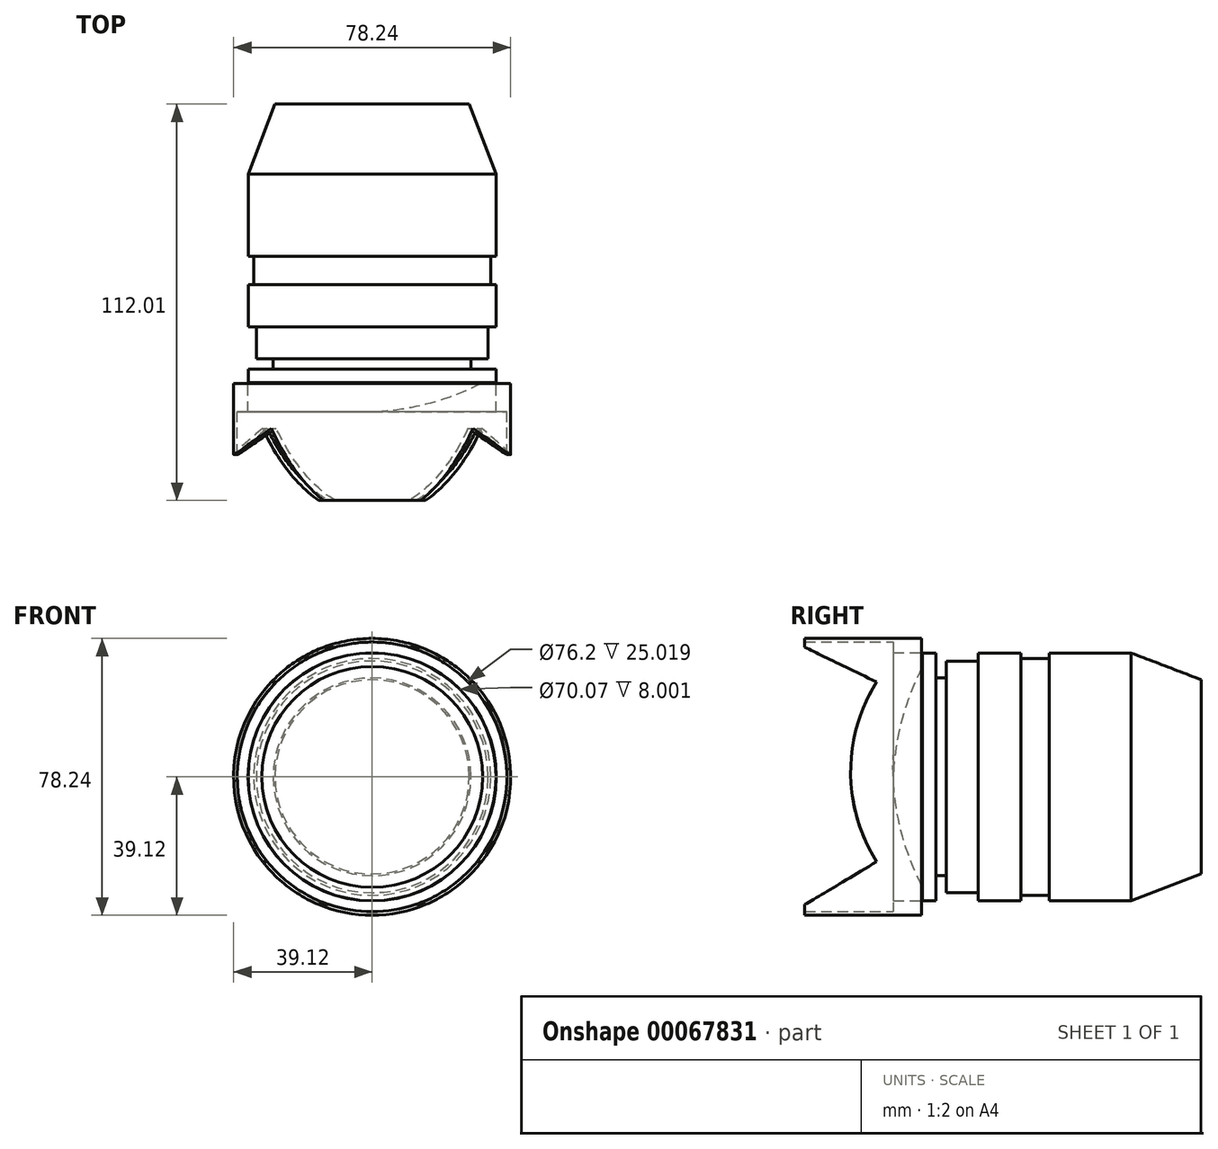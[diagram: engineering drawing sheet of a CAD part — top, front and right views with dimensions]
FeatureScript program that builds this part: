
annotation { "Feature Type Name" : "Feature", "Feature Type Description" : "" }
export const myFeature = defineFeature(function(context is Context, id is Id, definition is map)
    precondition{}
    {
        {
            var Q0;
            Q0=qCreatedBy(makeId("Top.planeOp"),FACE);
            var sketch = newSketch(context, id + "F0", { "sketchPlane" : qUnion([Q0])});
            skLineSegment(sketch, "E0.bottom", {"start": v(0, 0) * mm, "end": v(27.43, 0) * mm});
            skLineSegment(sketch, "E0.top", {"start": v(0, -19.81) * mm, "end": v(35, -19.81) * mm});
            skLineSegment(sketch, "E0.left", {"start": v(0, 0) * mm, "end": v(0, -19.81) * mm});
            skLineSegment(sketch, "E0.right", {"start": v(27.43, 0) * mm, "end": v(35, -19.81) * mm});
            skLineSegment(sketch, "E1.top", {"start": v(31.2, -78.74) * mm, "end": v(35, -78.74) * mm});
            skLineSegment(sketch, "E1.right", {"start": v(35, -19.81) * mm, "end": v(35, -78.74) * mm});
            skLineSegment(sketch, "E2.bottom", {"start": v(35, -78.74) * mm, "end": v(31.2, -78.74) * mm});
            skLineSegment(sketch, "E2.top", {"start": v(35, -87.12) * mm, "end": v(31.2, -87.12) * mm});
            skLineSegment(sketch, "E2.left", {"start": v(35, -78.74) * mm, "end": v(35, -87.12) * mm});
            skLineSegment(sketch, "E2.right", {"start": v(31.2, -78.74) * mm, "end": v(31.2, -87.12) * mm});
            skArc(sketch, "E3", {"start": v(0, -87.06) * mm, "mid": v(16.05, -84.61) * mm, "end": v(31.2, -78.74) * mm});
            skLineSegment(sketch, "E4", {"start": v(0, -19.81) * mm, "end": v(0, -87.06) * mm});
            skLineSegment(sketch, "E5", {"start": v(0, 0) * mm, "end": v(0, 75.81) * mm});
            skSolve(sketch);
        }
        {
            var Q0;
            Q0=qCreatedBy(makeId("Top.planeOp"),FACE);
            var sketch = newSketch(context, id + "F1", { "sketchPlane" : qUnion([Q0])});
            skLineSegment(sketch, "E6.top", {"start": v(38.1, -112.01) * mm, "end": v(39.12, -112.01) * mm});
            skLineSegment(sketch, "E6.right", {"start": v(39.12, -79) * mm, "end": v(39.12, -112.01) * mm});
            skLineSegment(sketch, "E7.bottom", {"start": v(39.12, -79) * mm, "end": v(35.04, -79) * mm});
            skLineSegment(sketch, "E7.top", {"start": v(38.1, -87) * mm, "end": v(35.04, -87) * mm});
            skLineSegment(sketch, "E7.right", {"start": v(35.04, -79) * mm, "end": v(35.04, -87) * mm});
            skLineSegment(sketch, "E8", {"start": v(0, -3.1) * mm, "end": v(0, -147) * mm});
            skLineSegment(sketch, "E9", {"start": v(38.1, -87) * mm, "end": v(38.1, -112.01) * mm});
            skLineSegment(sketch, "E10", {"start": v(35.04, -87) * mm, "end": v(38.1, -112.01) * mm});
            skPoint(sketch, "E11.orphan", {"position": v(38.1, -79) * mm});
            skSolve(sketch);
        }
        {
            var Q0;
            Q0=makeQuery(id+"F0.imprint","IMPRINT",FACE,{"disambiguationData":[TD([[makeQuery(id+"F0.imprint","IMPRINT",EDGE,{"derivedFrom":sQuery(id+"F0.wireOp",EDGE,"E0.bottom")}),-1.0]])]});
            var Q1;
            Q1=makeQuery(id+"F0.imprint","IMPRINT",FACE,{"disambiguationData":[TD([[makeQuery(id+"F0.imprint","IMPRINT",EDGE,{"derivedFrom":sQuery(id+"F0.wireOp",EDGE,"E0.top")}),-1.0]])]});
            var Q2;
            Q2=makeQuery(id+"F0.imprint","IMPRINT",FACE,{"disambiguationData":[TD([[makeQuery(id+"F0.imprint","IMPRINT",EDGE,{"derivedFrom":sQuery(id+"F0.wireOp",EDGE,"E2.bottom")}),1.0]])]});
            var Q3;
            Q3=makeQuery(id+"F1.imprint","IMPRINT",FACE,{"disambiguationData":[TD([[makeQuery(id+"F1.imprint","IMPRINT",EDGE,{"derivedFrom":sQuery(id+"F1.wireOp",EDGE,"E6.top")}),1.0]])]});
            var Q4;
            Q4=sQuery(id+"F1.wireOp",EDGE,"E8");
            revolve(context, id + "F2", {"entities" : qUnion([Q0, Q1, Q2, Q3]), "axis" : qUnion([Q4]), "revolveType" : RevolveType.FULL});
        }
        {
            var Q0;
            Q0=qCreatedBy(makeId("Right.planeOp"),FACE);
            var sketch = newSketch(context, id + "F3", { "sketchPlane" : qUnion([Q0])});
            skLineSegment(sketch, "E12", {"start": v(0, 0) * mm, "end": v(-158.43, 0) * mm});
            skLineSegment(sketch, "E13.bottom", {"start": v(-117.1, 0) * mm, "end": v(-117.1, 0) * mm});
            skLineSegment(sketch, "E13.right", {"start": v(-117.1, 0) * mm, "end": v(-117.1, 39.12) * mm});
            skLineSegment(sketch, "E14", {"start": v(-117.1, 39.12) * mm, "end": v(-91.7, 26.8) * mm});
            skLineSegment(sketch, "E15", {"start": v(-91.7, -23.96) * mm, "end": v(-117.1, -39.12) * mm});
            skLineSegment(sketch, "E16", {"start": v(-117.1, -39.12) * mm, "end": v(-117.1, 0) * mm});
            skArc(sketch, "E17", {"start": v(-91.7, 26.8) * mm, "mid": v(-99.08, 1.42) * mm, "end": v(-91.7, -23.96) * mm});
            skSolve(sketch);
        }
        {
            var Q0;
            Q0 = qSketchRegion(id + "F3", true);
            extrude(context, id + "F4", {"entities" : qUnion([Q0]), "operationType" : NewBodyOperationType.REMOVE, "oppositeDirection" : true, "depth" : 50.8 * mm, "hasSecondDirection" : true, "secondDirectionOppositeDirection" : false, "secondDirectionDepth" : 50.8 * mm});
        }
        {
            var Q0;
            Q0=qCreatedBy(makeId("Top.planeOp"),FACE);
            var sketch = newSketch(context, id + "F5", { "sketchPlane" : qUnion([Q0])});
            skLineSegment(sketch, "E18.bottom", {"start": v(32.74, -63) * mm, "end": v(46.75, -63) * mm});
            skLineSegment(sketch, "E18.top", {"start": v(32.74, -72) * mm, "end": v(46.75, -72) * mm});
            skLineSegment(sketch, "E18.left", {"start": v(32.74, -63) * mm, "end": v(32.74, -72) * mm});
            skLineSegment(sketch, "E18.right", {"start": v(46.75, -63) * mm, "end": v(46.75, -72) * mm});
            skLineSegment(sketch, "E19.bottom", {"start": v(35.5, -51) * mm, "end": v(46.75, -51) * mm});
            skLineSegment(sketch, "E19.top", {"start": v(35.5, -63) * mm, "end": v(46.75, -63) * mm});
            skLineSegment(sketch, "E19.left", {"start": v(35.5, -51) * mm, "end": v(35.5, -63) * mm});
            skLineSegment(sketch, "E19.right", {"start": v(46.75, -51) * mm, "end": v(46.75, -63) * mm});
            skLineSegment(sketch, "E20.bottom", {"start": v(33.48, -43) * mm, "end": v(46.75, -43) * mm});
            skLineSegment(sketch, "E20.top", {"start": v(33.48, -51) * mm, "end": v(46.75, -51) * mm});
            skLineSegment(sketch, "E20.left", {"start": v(33.48, -43) * mm, "end": v(33.48, -51) * mm});
            skLineSegment(sketch, "E20.right", {"start": v(46.75, -43) * mm, "end": v(46.75, -51) * mm});
            skLineSegment(sketch, "E21.bottom", {"start": v(46.75, -72) * mm, "end": v(27.94, -72) * mm});
            skLineSegment(sketch, "E21.top", {"start": v(46.75, -74.93) * mm, "end": v(27.94, -74.93) * mm});
            skLineSegment(sketch, "E21.left", {"start": v(46.75, -72) * mm, "end": v(46.75, -74.93) * mm});
            skLineSegment(sketch, "E21.right", {"start": v(27.94, -72) * mm, "end": v(27.94, -74.93) * mm});
            skLineSegment(sketch, "E22", {"start": v(0, -1.22) * mm, "end": v(0, -130.27) * mm});
            skSolve(sketch);
        }
        {
            var Q0;
            Q0 = qSketchRegion(id + "F5", true);
            var Q1;
            Q1=sQuery(id+"F5.wireOp",EDGE,"E22");
            revolve(context, id + "F6", {"operationType" : NewBodyOperationType.REMOVE, "entities" : qUnion([Q0]), "axis" : qUnion([Q1]), "revolveType" : RevolveType.FULL, "oppositeDirection" : true});
        }
    });
